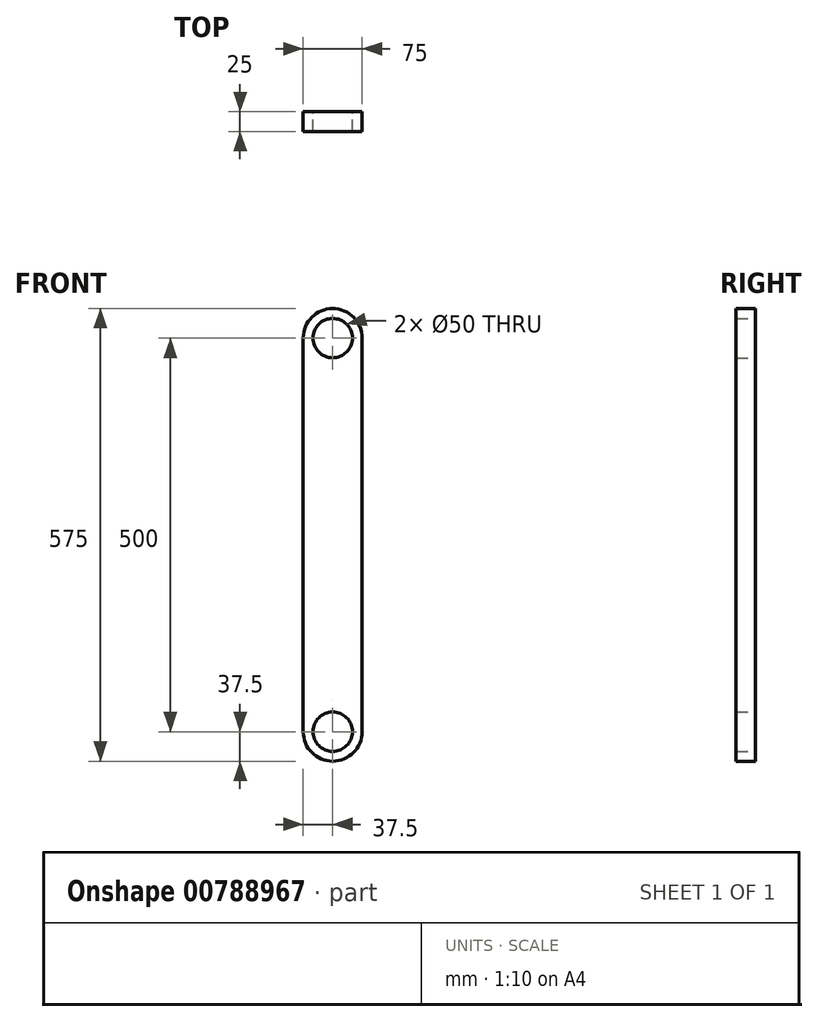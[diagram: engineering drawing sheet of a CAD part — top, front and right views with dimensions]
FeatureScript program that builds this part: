
annotation { "Feature Type Name" : "Feature", "Feature Type Description" : "" }
export const myFeature = defineFeature(function(context is Context, id is Id, definition is map)
    precondition{}
    {
        {
            var Q0;
            Q0=qCreatedBy(makeId("Front.planeOp"),FACE);
            var sketch = newSketch(context, id + "F0", { "sketchPlane" : qUnion([Q0])});
            skCircle(sketch, "E0", {"center": v(0, 0) * mm, "radius": 37.5 * mm});
            skLineSegment(sketch, "E1", {"start": v(-37.5, 0) * mm, "end": v(-37.5, 500) * mm});
            skLineSegment(sketch, "E2", {"start": v(37.5, 0) * mm, "end": v(37.5, 500) * mm});
            skLineSegment(sketch, "E3", {"start": v(-37.5, 500) * mm, "end": v(37.5, 500) * mm, "construction": true});
            skCircle(sketch, "E4", {"center": v(0, 0) * mm, "radius": 25 * mm});
            skCircle(sketch, "E5", {"center": v(0, 500) * mm, "radius": 37.5 * mm});
            skCircle(sketch, "E6", {"center": v(0, 500) * mm, "radius": 25 * mm});
            skSolve(sketch);
        }
        {
            var Q0;
            Q0=makeQuery(id+"F0.imprint","IMPRINT",FACE,{"disambiguationData":[TD([[makeQuery(id+"F0.imprint","IMPRINT",EDGE,{"derivedFrom":sQuery(id+"F0.wireOp",EDGE,"E4")}),-1.0]])]});
            var Q1;
            Q1=makeQuery(id+"F0.imprint","IMPRINT",FACE,{"disambiguationData":[TD([[makeQuery(id+"F0.imprint","IMPRINT",EDGE,{"derivedFrom":sQuery(id+"F0.wireOp",EDGE,"E6")}),-1.0]])]});
            var Q2;
            {var subQ0=sQuery(id+"F0.wireOp",EDGE,"E1");Q2=makeQuery(id+"F0.imprint","IMPRINT",FACE,{"disambiguationData":[TD([[makeQuery(id+"F0.imprint","IMPRINT",EDGE,{"derivedFrom":subQ0}),-1.0]])]});}
            extrude(context, id + "F1", {"entities" : qUnion([Q0, Q1, Q2]), "depth" : 25 * mm, "offsetDistance" : 25 * mm});
        }
    });
